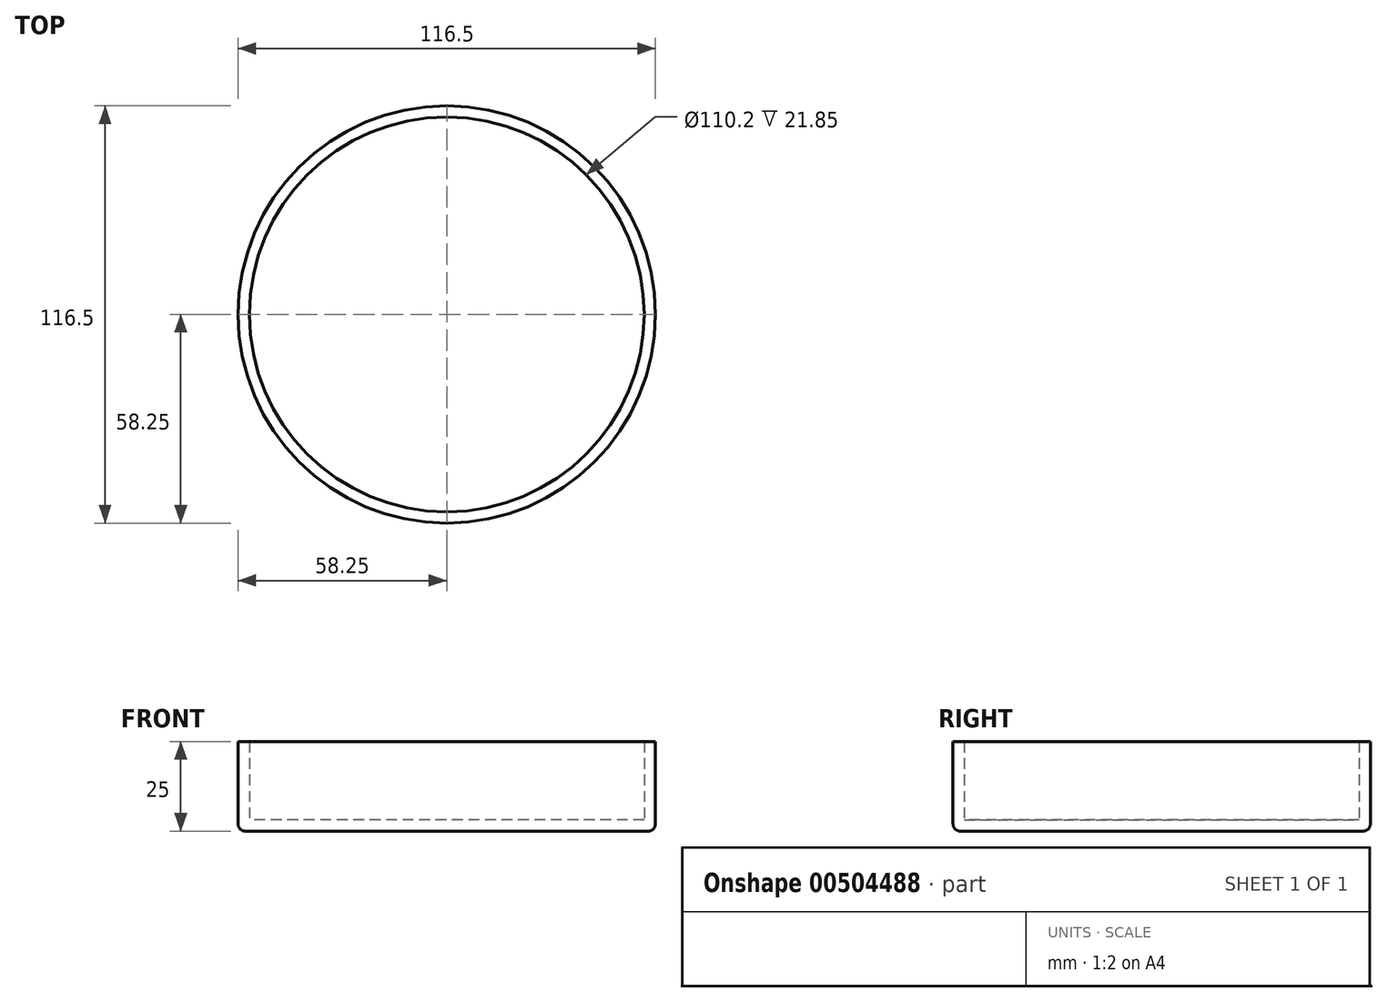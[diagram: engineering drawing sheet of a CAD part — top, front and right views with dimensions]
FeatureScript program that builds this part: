
annotation { "Feature Type Name" : "Feature", "Feature Type Description" : "" }
export const myFeature = defineFeature(function(context is Context, id is Id, definition is map)
    precondition{}
    {
        {
            var Q0;
            Q0=qCreatedBy(makeId("Top.planeOp"),FACE);
            var sketch = newSketch(context, id + "F0", { "sketchPlane" : qUnion([Q0])});
            skCircle(sketch, "E0", {"center": v(0, 0) * mm, "radius": 58.25 * mm});
            skSolve(sketch);
        }
        {
            var Q0;
            Q0 = qSketchRegion(id + "F0", true);
            extrude(context, id + "F1", {"entities" : qUnion([Q0]), "depth" : 25 * mm, "offsetDistance" : 25 * mm});
        }
        {
            var Q0;
            Q0=makeQuery(id+"F1.opExtrude","CAP_FACE",FACE,{"disambiguationData":[OSD([sQuery(id+"F0.wireOp",EDGE,"E0")])],"isStart":false});
            shell(context, id + "F2", {"entities" : qUnion([Q0]), "thickness" : 3.15 * mm});
        }
        {
            var Q0;
            Q0=makeQuery(id+"F1.opExtrude","CAP_EDGE",EDGE,{"disambiguationData":[OSD([sQuery(id+"F0.wireOp",EDGE,"E0")])],"isStart":true});
            fillet(context, id + "F3", {"entities" : qUnion([Q0]), "radius" : 2 * mm, "tangentPropagation" : true, "allowEdgeOverflow" : false});
        }
    });
